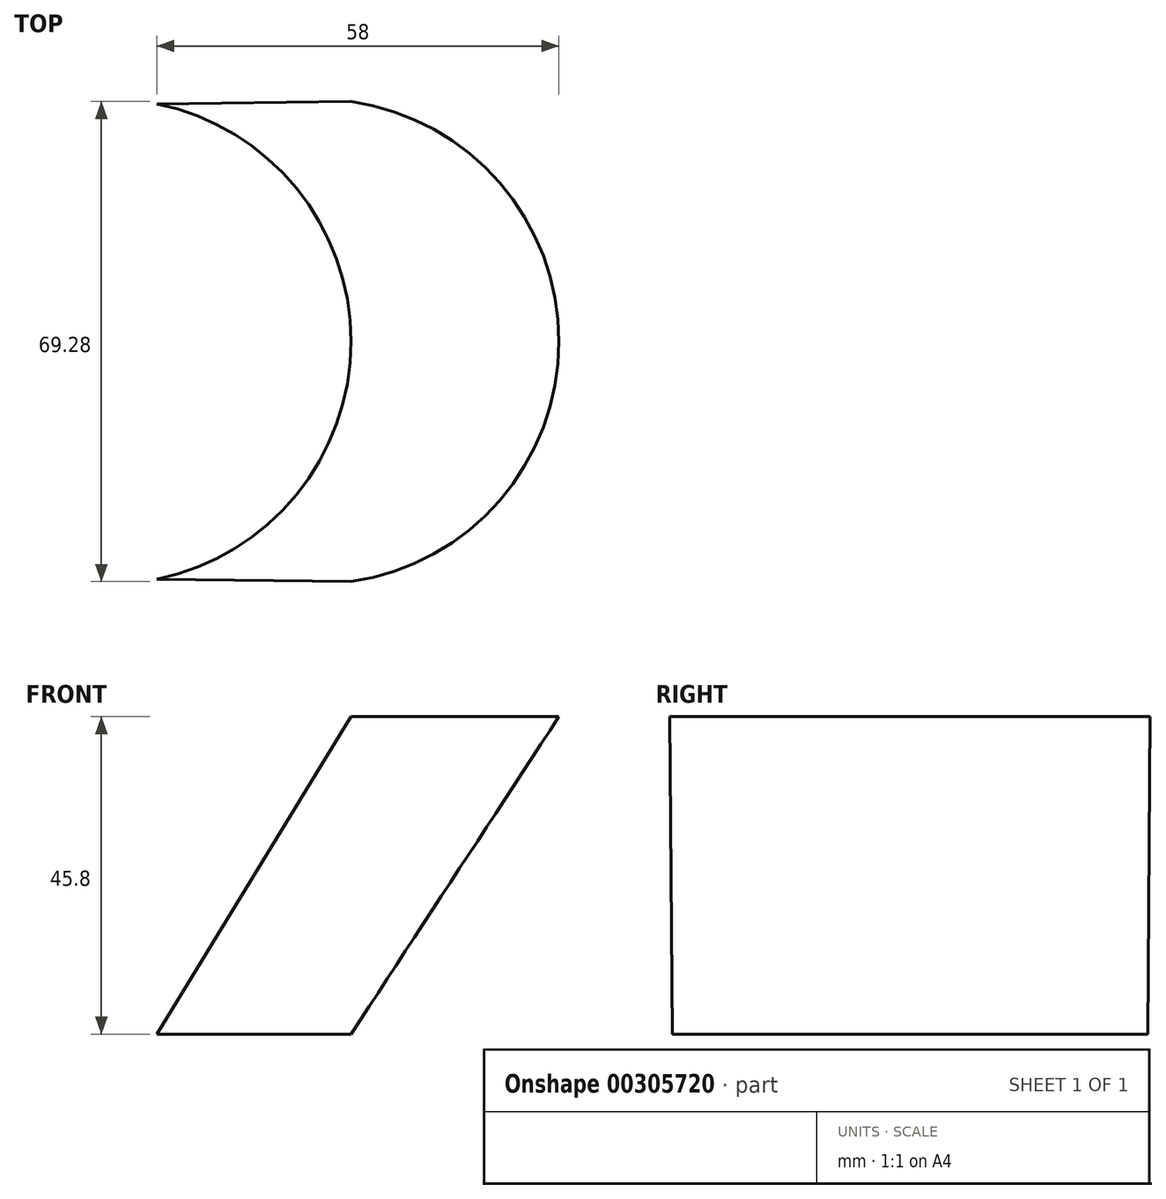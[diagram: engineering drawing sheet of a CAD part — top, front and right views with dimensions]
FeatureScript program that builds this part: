
annotation { "Feature Type Name" : "Feature", "Feature Type Description" : "" }
export const myFeature = defineFeature(function(context is Context, id is Id, definition is map)
    precondition{}
    {
        {
            var Q0;
            Q0=qCreatedBy(makeId("Top.planeOp"),FACE);
            var sketch = newSketch(context, id + "F0", { "sketchPlane" : qUnion([Q0])});
            skArc(sketch, "E0", {"start": v(7, -34.3) * mm, "mid": v(35, 0) * mm, "end": v(7, 34.3) * mm});
            skLineSegment(sketch, "E1", {"start": v(7, 34.3) * mm, "end": v(7, -34.3) * mm, "construction": true});
            skSolve(sketch);
        }
        {
            var Q0;
            Q0=qCreatedBy(makeId("Top.planeOp"),FACE);
            cPlane(context, id + "F1", {"entities" : qUnion([Q0]), "cplaneType" : CPlaneType.OFFSET, "offset" : 45.8 * mm, "width" : 150 * mm, "height" : 150 * mm});
        }
        {
            var Q0;
            Q0=qCreatedBy(id+"F1.planeOp",FACE);
            var sketch = newSketch(context, id + "F2", { "sketchPlane" : qUnion([Q0])});
            skArc(sketch, "E2", {"start": v(35, -34.64) * mm, "mid": v(65, 0) * mm, "end": v(35, 34.64) * mm});
            skLineSegment(sketch, "E3", {"start": v(35, 34.64) * mm, "end": v(35, -34.64) * mm, "construction": true});
            skSolve(sketch);
        }
        {
            var Q0;
            Q0=sQuery(id+"F2.wireOp",EDGE,"E2");
            var Q1;
            Q1=sQuery(id+"F0.wireOp",EDGE,"E0");
            loft(context, id + "F3", {"bodyType" : ToolBodyType.SURFACE, "operationType" : NewBodyOperationType.ADD, "wireProfilesArray" : [{ "wireProfileEntities" : qUnion([Q0]) }, { "wireProfileEntities" : qUnion([Q1]) }]});
        }
    });
